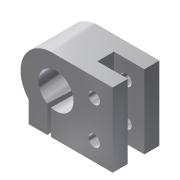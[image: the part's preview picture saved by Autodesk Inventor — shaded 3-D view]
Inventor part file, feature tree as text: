
AUTODESK INVENTOR PART (.ipt)
format: ipt  version: 2015 (Build 190159000, 159)  size: 168,960 bytes
history: native  units: mm
features: sketch x4, extrude x3, revolve x1
ambient origin geometry x8: Origin, YZ Plane, XZ Plane, XY Plane, X Axis, Y Axis, Z Axis, Center Point
bodies: Solid1 (feature_tree)
feature tree (8):
  extrude  "Extrusion1"  Depth=40.0mm
  extrude  "Extrusion2"  Depth=10.0mm
  revolve  "Revolution1"  [1 undecoded]
  extrude  "Extrusion3"  Depth=45.5mm
  sketch  "Sketch1"  dims[d0=50.0mm d1=40.0mm]
  sketch  "Sketch2"  dims[d2=10.0mm d3=10.0mm]
  sketch  "Sketch5"  dims[d4=20.0mm d5=6.2mm]
  sketch  "Sketch6"  dims[d6=6.2mm d7=45.5mm d8=35.5mm d9=4.5mm d10=4.5mm d13=12.5mm d14=12.5mm d15=2.0mm d16=25.4mm d17=0.0mm d18=8.2mm d19=16.5mm d20=9.0mm d21=25.4mm d22=0.0mm d23=10.0mm d25=9.5mm d26=30.543262mm d27=10.0mm d28=19.0mm d29=30.0mm d30=90.0deg d31=19.0mm d32=90.0deg d33=10.0mm d34=0.0mm]
note: 1 required parameter value undecoded (feature->parameter linkage not recoverable at this tier; creation-order binding heuristic only, values carry confidence <= 0.55)
